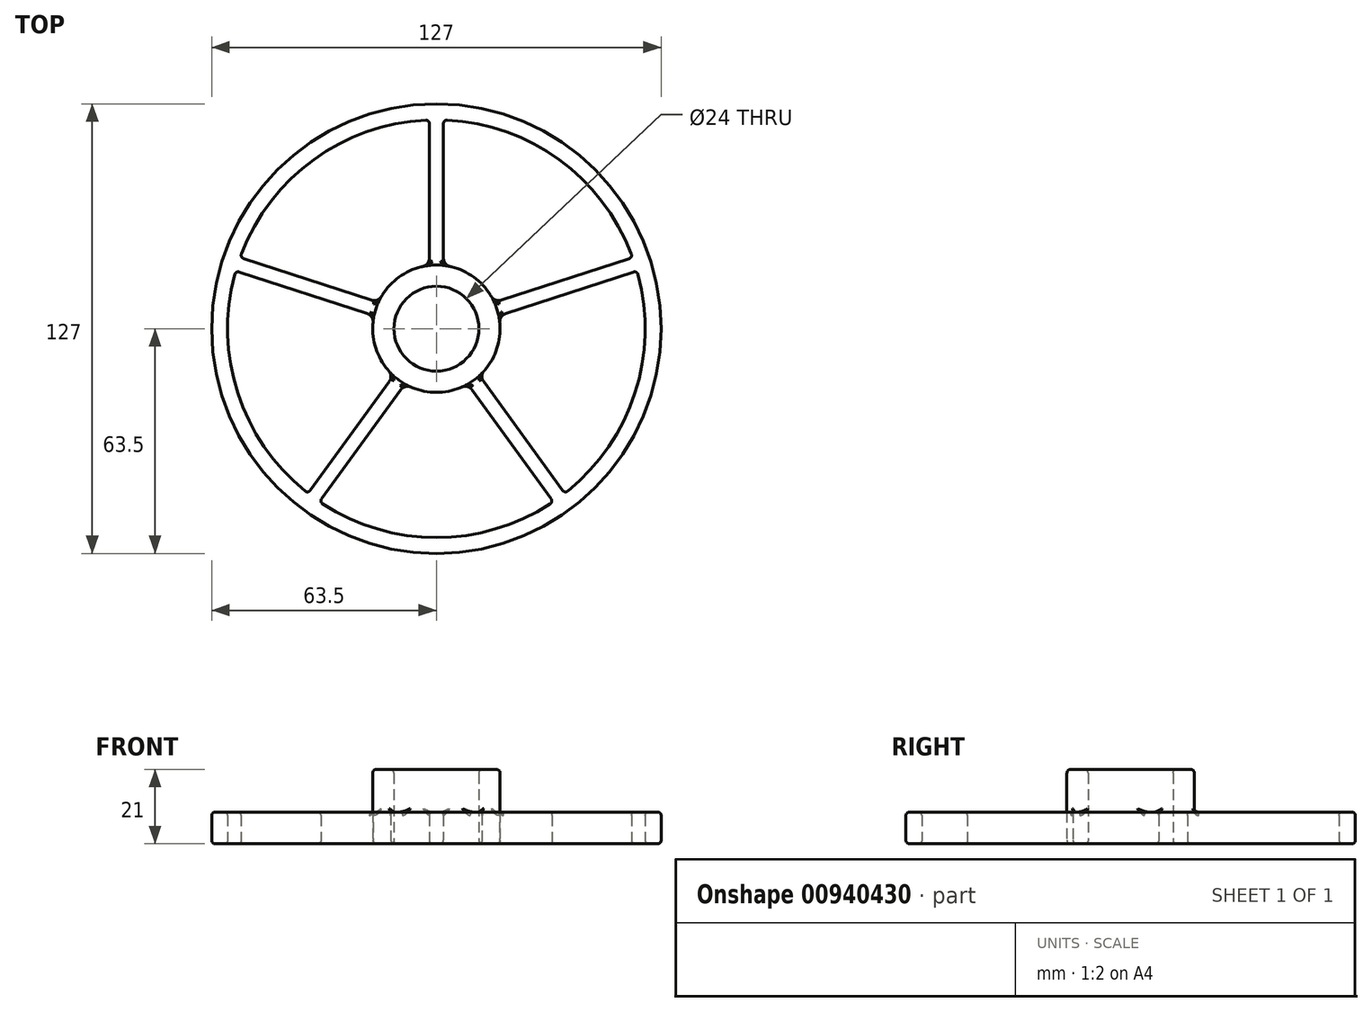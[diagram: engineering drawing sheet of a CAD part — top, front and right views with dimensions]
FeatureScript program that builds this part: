
annotation { "Feature Type Name" : "Feature", "Feature Type Description" : "" }
export const myFeature = defineFeature(function(context is Context, id is Id, definition is map)
    precondition{}
    {
        {
            var Q0;
            Q0=qCreatedBy(makeId("Top.planeOp"),FACE);
            var sketch = newSketch(context, id + "F0", { "sketchPlane" : qUnion([Q0])});
            skCircle(sketch, "E0", {"center": v(0, 0) * mm, "radius": 12 * mm});
            skCircle(sketch, "E1", {"center": v(0, 0) * mm, "radius": 63.5 * mm});
            skArc(sketch, "E2", {"start": v(-2, 58.97) * mm, "mid": v(-34.68, 47.73) * mm, "end": v(-55.46, 20.12) * mm});
            skLineSegment(sketch, "E3.left", {"start": v(-2, 58.97) * mm, "end": v(-2, 19.9) * mm});
            skLineSegment(sketch, "E3.right", {"start": v(2, 58.97) * mm, "end": v(2, 19.92) * mm});
            skPoint(sketch, "E3.middle", {"position": v(0, 38.97) * mm});
            skPoint(sketch, "E4", {"position": v(-2, 19.9) * mm});
            skPoint(sketch, "E5", {"position": v(2, 19.92) * mm});
            skPoint(sketch, "E3.top.start.orphan", {"position": v(-2, 18.97) * mm});
            skPoint(sketch, "E6.orphan", {"position": v(2, 18.97) * mm});
            skLineSegment(sketch, "E7.1.0", {"start": v(-56.7, 16.32) * mm, "end": v(-19.54, 4.25) * mm});
            skLineSegment(sketch, "E7.1.1", {"start": v(-55.46, 20.12) * mm, "end": v(-18.33, 8.06) * mm});
            skLineSegment(sketch, "E7.2.0", {"start": v(-33.04, -48.88) * mm, "end": v(-10.08, -17.27) * mm});
            skLineSegment(sketch, "E7.2.1", {"start": v(-36.28, -46.53) * mm, "end": v(-13.33, -14.94) * mm});
            skLineSegment(sketch, "E7.3.0", {"start": v(36.28, -46.53) * mm, "end": v(13.31, -14.92) * mm});
            skLineSegment(sketch, "E7.3.1", {"start": v(33.04, -48.88) * mm, "end": v(10.1, -17.3) * mm});
            skLineSegment(sketch, "E7.4.0", {"start": v(55.46, 20.12) * mm, "end": v(18.3, 8.05) * mm});
            skLineSegment(sketch, "E7.4.1", {"start": v(56.7, 16.32) * mm, "end": v(19.56, 4.25) * mm});
            skArc(sketch, "E8", {"start": v(-17.89, 2.02) * mm, "mid": v(-17.12, -5.56) * mm, "end": v(-13.28, -12.15) * mm});
            skArc(sketch, "E9", {"start": v(2, 19.92) * mm, "mid": v(2.63, 18.28) * mm, "end": v(4.2, 17.5) * mm});
            skArc(sketch, "E10.MirrorCS", {"start": v(-2, 19.92) * mm, "mid": v(-2.63, 18.28) * mm, "end": v(-4.2, 17.5) * mm});
            skArc(sketch, "E11.1.0", {"start": v(-18.33, 8.06) * mm, "mid": v(-16.57, 8.16) * mm, "end": v(-15.35, 9.4) * mm});
            skArc(sketch, "E11.1.1", {"start": v(-19.56, 4.25) * mm, "mid": v(-18.2, 3.14) * mm, "end": v(-17.94, 1.4) * mm});
            skArc(sketch, "E11.2.0", {"start": v(-13.33, -14.94) * mm, "mid": v(-12.88, -13.24) * mm, "end": v(-13.69, -11.69) * mm});
            skArc(sketch, "E11.2.1", {"start": v(-10.1, -17.3) * mm, "mid": v(-8.62, -16.34) * mm, "end": v(-6.89, -16.63) * mm});
            skArc(sketch, "E11.3.0", {"start": v(10.1, -17.3) * mm, "mid": v(8.62, -16.34) * mm, "end": v(6.89, -16.63) * mm});
            skArc(sketch, "E11.3.1", {"start": v(13.33, -14.94) * mm, "mid": v(12.88, -13.24) * mm, "end": v(13.69, -11.69) * mm});
            skArc(sketch, "E11.4.0", {"start": v(19.56, 4.25) * mm, "mid": v(18.2, 3.14) * mm, "end": v(17.94, 1.4) * mm});
            skArc(sketch, "E11.4.1", {"start": v(18.33, 8.06) * mm, "mid": v(16.57, 8.16) * mm, "end": v(15.35, 9.4) * mm});
            skPoint(sketch, "E12", {"position": v(-15.35, 9.4) * mm});
            skPoint(sketch, "E13", {"position": v(-17.94, 1.4) * mm});
            skPoint(sketch, "E14", {"position": v(-4.2, 17.5) * mm});
            skPoint(sketch, "E15", {"position": v(4.2, 17.5) * mm});
            skArc(sketch, "E16.trimOffspring", {"start": v(-3.6, 17.64) * mm, "mid": v(-10.58, 14.56) * mm, "end": v(-15.66, 8.88) * mm});
            skPoint(sketch, "E17", {"position": v(15.35, 9.4) * mm});
            skPoint(sketch, "E18", {"position": v(17.94, 1.4) * mm});
            skArc(sketch, "E19.trimOffspring", {"start": v(15.66, 8.88) * mm, "mid": v(10.58, 14.56) * mm, "end": v(3.6, 17.64) * mm});
            skPoint(sketch, "E20", {"position": v(-13.69, -11.69) * mm});
            skPoint(sketch, "E21", {"position": v(-6.89, -16.63) * mm});
            skArc(sketch, "E22.trimOffspring", {"start": v(-7.45, -16.39) * mm, "mid": v(0, -18) * mm, "end": v(7.45, -16.39) * mm});
            skPoint(sketch, "E23", {"position": v(13.69, -11.69) * mm});
            skPoint(sketch, "E24", {"position": v(6.89, -16.63) * mm});
            skArc(sketch, "E25.trimOffspring", {"start": v(13.28, -12.15) * mm, "mid": v(17.12, -5.56) * mm, "end": v(17.89, 2.02) * mm});
            skArc(sketch, "E26.trimOffspring", {"start": v(55.46, 20.12) * mm, "mid": v(34.68, 47.73) * mm, "end": v(2, 58.97) * mm});
            skArc(sketch, "E27.trimOffspring", {"start": v(36.28, -46.53) * mm, "mid": v(56.11, -18.23) * mm, "end": v(56.7, 16.32) * mm});
            skArc(sketch, "E28.trimOffspring", {"start": v(-33.04, -48.88) * mm, "mid": v(0, -59) * mm, "end": v(33.04, -48.88) * mm});
            skArc(sketch, "E29.trimOffspring", {"start": v(-56.7, 16.32) * mm, "mid": v(-56.11, -18.23) * mm, "end": v(-36.28, -46.53) * mm});
            skSolve(sketch);
        }
        {
            var Q0;
            Q0=makeQuery(id+"F0.imprint","IMPRINT",FACE,{"disambiguationData":[TD([[makeQuery(id+"F0.imprint","IMPRINT",EDGE,{"derivedFrom":sQuery(id+"F0.wireOp",EDGE,"E1")}),1.0]])]});
            var Q1;
            Q1=makeQuery(id+"F0.imprint","IMPRINT",FACE,{"disambiguationData":[TD([[makeQuery(id+"F0.imprint","IMPRINT",EDGE,{"derivedFrom":sQuery(id+"F0.wireOp",EDGE,"E3.bottom")}),-1.0]])]});
            var Q2;
            {var subQ5=sQuery(id+"F0.wireOp",EDGE,"E7.4.0");Q2=makeQuery(id+"F0.imprint","IMPRINT",FACE,{"disambiguationData":[TD([[makeQuery(id+"F0.imprint","IMPRINT",EDGE,{"derivedFrom":subQ5}),1.0]])]});}
            var Q3;
            {var subQ0=sQuery(id+"F0.wireOp",EDGE,"E7.3.0");Q3=makeQuery(id+"F0.imprint","IMPRINT",FACE,{"disambiguationData":[TD([[makeQuery(id+"F0.imprint","IMPRINT",EDGE,{"derivedFrom":subQ0}),1.0]])]});}
            var Q4;
            {var subQ5=sQuery(id+"F0.wireOp",EDGE,"E7.2.0");Q4=makeQuery(id+"F0.imprint","IMPRINT",FACE,{"disambiguationData":[TD([[makeQuery(id+"F0.imprint","IMPRINT",EDGE,{"derivedFrom":subQ5}),1.0]])]});}
            var Q5;
            {var subQ5=sQuery(id+"F0.wireOp",EDGE,"E7.1.0");Q5=makeQuery(id+"F0.imprint","IMPRINT",FACE,{"disambiguationData":[TD([[makeQuery(id+"F0.imprint","IMPRINT",EDGE,{"derivedFrom":subQ5}),1.0]])]});}
            var Q6;
            Q6=makeQuery(id+"F0.imprint","IMPRINT",FACE,{"disambiguationData":[TD([[makeQuery(id+"F0.imprint","IMPRINT",EDGE,{"derivedFrom":sQuery(id+"F0.wireOp",EDGE,"E0")}),-1.0]])]});
            extrude(context, id + "F1", {"entities" : qUnion([Q0, Q1, Q2, Q3, Q4, Q5, Q6]), "depth" : 9 * mm, "offsetDistance" : 25 * mm});
        }
        {
            var Q0;
            Q0=makeQuery(id+"F1.opExtrude","CAP_FACE",FACE,{"disambiguationData":[OSD([sQuery(id+"F0.wireOp",EDGE,"E0"),sQuery(id+"F0.wireOp",EDGE,"E1"),sQuery(id+"F0.wireOp",EDGE,"E2"),sQuery(id+"F0.wireOp",EDGE,"E3.left"),sQuery(id+"F0.wireOp",EDGE,"E3.right"),sQuery(id+"F0.wireOp",EDGE,"E7.1.0"),sQuery(id+"F0.wireOp",EDGE,"E7.1.1"),sQuery(id+"F0.wireOp",EDGE,"E7.2.0"),sQuery(id+"F0.wireOp",EDGE,"E7.2.1"),sQuery(id+"F0.wireOp",EDGE,"E7.3.0"),sQuery(id+"F0.wireOp",EDGE,"E7.3.1"),sQuery(id+"F0.wireOp",EDGE,"E7.4.0"),sQuery(id+"F0.wireOp",EDGE,"E7.4.1"),sQuery(id+"F0.wireOp",EDGE,"E8"),sQuery(id+"F0.wireOp",EDGE,"E9"),sQuery(id+"F0.wireOp",EDGE,"E10.MirrorCS"),sQuery(id+"F0.wireOp",EDGE,"E11.1.0"),sQuery(id+"F0.wireOp",EDGE,"E11.1.1"),sQuery(id+"F0.wireOp",EDGE,"E11.2.0"),sQuery(id+"F0.wireOp",EDGE,"E11.2.1"),sQuery(id+"F0.wireOp",EDGE,"E11.3.0"),sQuery(id+"F0.wireOp",EDGE,"E11.3.1"),sQuery(id+"F0.wireOp",EDGE,"E11.4.0"),sQuery(id+"F0.wireOp",EDGE,"E11.4.1"),sQuery(id+"F0.wireOp",EDGE,"E16.trimOffspring"),sQuery(id+"F0.wireOp",EDGE,"E19.trimOffspring"),sQuery(id+"F0.wireOp",EDGE,"E22.trimOffspring"),sQuery(id+"F0.wireOp",EDGE,"E25.trimOffspring"),sQuery(id+"F0.wireOp",EDGE,"E26.trimOffspring"),sQuery(id+"F0.wireOp",EDGE,"E27.trimOffspring"),sQuery(id+"F0.wireOp",EDGE,"E28.trimOffspring"),sQuery(id+"F0.wireOp",EDGE,"E29.trimOffspring")])],"isStart":false});
            var sketch = newSketch(context, id + "F2", { "sketchPlane" : qUnion([Q0])});
            skCircle(sketch, "E30", {"center": v(0, 0) * mm, "radius": 18 * mm});
            skSolve(sketch);
        }
        {
            var Q0;
            Q0=makeQuery(id+"F2.imprint","IMPRINT",FACE,{"disambiguationData":[TD([[makeQuery(id+"F2.imprint","IMPRINT",EDGE,{"derivedFrom":makeQuery(id+"F1.opExtrude","CAP_EDGE",EDGE,{"disambiguationData":[OSD([sQuery(id+"F0.wireOp",EDGE,"E0")])],"isStart":false})}),-1.0]])]});
            extrude(context, id + "F3", {"entities" : qUnion([Q0]), "operationType" : NewBodyOperationType.ADD, "depth" : 12 * mm, "offsetDistance" : 25 * mm});
        }
        {
            var Q0;
            Q0=makeQuery(id+"F1.opExtrude","SWEPT_FACE",FACE,{"disambiguationData":[OSD([sQuery(id+"F0.wireOp",EDGE,"E7.4.0")])]});
            var Q1;
            Q1=makeQuery(id+"F1.opExtrude","CAP_EDGE",EDGE,{"disambiguationData":[OSD([sQuery(id+"F0.wireOp",EDGE,"E29.trimOffspring")])],"isStart":false});
            var Q2;
            Q2=makeQuery(id+"F1.opExtrude","CAP_EDGE",EDGE,{"disambiguationData":[OSD([sQuery(id+"F0.wireOp",EDGE,"E7.1.1")])],"isStart":false});
            var Q3;
            Q3=makeQuery(id+"F1.opExtrude","CAP_EDGE",EDGE,{"disambiguationData":[OSD([sQuery(id+"F0.wireOp",EDGE,"E1")])],"isStart":false});
            var Q4;
            Q4=makeQuery(id+"F1.opExtrude","CAP_EDGE",EDGE,{"disambiguationData":[OSD([sQuery(id+"F0.wireOp",EDGE,"E7.1.0")])],"isStart":false});
            var Q5;
            Q5=makeQuery(id+"F1.opExtrude","SWEPT_FACE",FACE,{"disambiguationData":[OSD([sQuery(id+"F0.wireOp",EDGE,"E29.trimOffspring")])]});
            var Q6;
            Q6=makeQuery(id+"F1.opExtrude","SWEPT_FACE",FACE,{"disambiguationData":[OSD([sQuery(id+"F0.wireOp",EDGE,"E7.1.1")])]});
            var Q7;
            Q7=makeQuery(id+"F1.opExtrude","CAP_EDGE",EDGE,{"disambiguationData":[OSD([sQuery(id+"F0.wireOp",EDGE,"E7.4.1")])],"isStart":false});
            var Q8;
            {var subQ0=sQuery(id+"F2.wireOp",EDGE,"E30");Q8=makeQuery(id+"F3.boolean.opBoolean","MERGE",FACE,{"derivedFrom":[makeQuery(id+"F1.opExtrude","SWEPT_FACE",FACE,{"disambiguationData":[OSD([sQuery(id+"F0.wireOp",EDGE,"E25.trimOffspring")])]}),makeQuery(id+"F3.opExtrude","SWEPT_FACE",FACE,{"disambiguationData":[OSD([subQ0]),TDD([makeQuery(id+"F2.imprint","IMPRINT",EDGE,{"disambiguationData":[TD([[makeQuery(id+"F2.imprint","INTERSECT",VERTEX,{"disambiguationData":[OD(0.0)],"derivedFrom":[makeQuery(id+"F1.opExtrude","CAP_EDGE",EDGE,{"disambiguationData":[OSD([sQuery(id+"F0.wireOp",EDGE,"E11.3.1")])],"isStart":false}),subQ0]}),-1.0]])],"derivedFrom":subQ0})])]})]});}
            var Q9;
            Q9=makeQuery(id+"F1.opExtrude","SWEPT_FACE",FACE,{"disambiguationData":[OSD([sQuery(id+"F0.wireOp",EDGE,"E7.2.1")])]});
            var Q10;
            Q10=makeQuery(id+"F1.opExtrude","CAP_EDGE",EDGE,{"disambiguationData":[OSD([sQuery(id+"F0.wireOp",EDGE,"E2")])],"isStart":false});
            var Q11;
            Q11=makeQuery(id+"F1.opExtrude","SWEPT_FACE",FACE,{"disambiguationData":[OSD([sQuery(id+"F0.wireOp",EDGE,"E3.left")])]});
            var Q12;
            Q12=makeQuery(id+"F1.opExtrude","CAP_EDGE",EDGE,{"disambiguationData":[OSD([sQuery(id+"F0.wireOp",EDGE,"E27.trimOffspring")])],"isStart":false});
            var Q13;
            Q13=makeQuery(id+"F1.opExtrude","SWEPT_FACE",FACE,{"disambiguationData":[OSD([sQuery(id+"F0.wireOp",EDGE,"E7.3.0")])]});
            var Q14;
            Q14=makeQuery(id+"F1.opExtrude","CAP_EDGE",EDGE,{"disambiguationData":[OSD([sQuery(id+"F0.wireOp",EDGE,"E26.trimOffspring")])],"isStart":false});
            var Q15;
            Q15=makeQuery(id+"F1.opExtrude","SWEPT_FACE",FACE,{"disambiguationData":[OSD([sQuery(id+"F0.wireOp",EDGE,"E3.right")])]});
            var Q16;
            {var subQ0=sQuery(id+"F2.wireOp",EDGE,"E30");Q16=makeQuery(id+"F3.opExtrude","SWEPT_FACE",FACE,{"disambiguationData":[OSD([subQ0]),TDD([makeQuery(id+"F2.imprint","IMPRINT",EDGE,{"disambiguationData":[TD([[makeQuery(id+"F2.imprint","INTERSECT",VERTEX,{"disambiguationData":[OD(1.0)],"derivedFrom":[makeQuery(id+"F1.opExtrude","CAP_EDGE",EDGE,{"disambiguationData":[OSD([sQuery(id+"F0.wireOp",EDGE,"E11.1.0")])],"isStart":false}),subQ0]}),-1.0]])],"derivedFrom":subQ0})])]});}
            var Q17;
            Q17=makeQuery(id+"F1.opExtrude","SWEPT_FACE",FACE,{"disambiguationData":[OSD([sQuery(id+"F0.wireOp",EDGE,"E7.1.0")])]});
            var Q18;
            Q18=makeQuery(id+"F1.opExtrude","SWEPT_FACE",FACE,{"disambiguationData":[OSD([sQuery(id+"F0.wireOp",EDGE,"E2")])]});
            var Q19;
            {var subQ0=sQuery(id+"F0.wireOp",EDGE,"E11.4.0");Q19=makeQuery(id+"F3.boolean.opBoolean","MERGE",FACE,{"derivedFrom":[makeQuery(id+"F1.opExtrude","SWEPT_FACE",FACE,{"disambiguationData":[OSD([subQ0])]}),makeQuery(id+"F3.opExtrude","SWEPT_FACE",FACE,{"disambiguationData":[OSD([subQ0])]})]});}
            var Q20;
            Q20=makeQuery(id+"F1.opExtrude","CAP_EDGE",EDGE,{"disambiguationData":[OSD([sQuery(id+"F0.wireOp",EDGE,"E3.left")])],"isStart":false});
            var Q21;
            Q21=makeQuery(id+"F3.opExtrude","CAP_FACE",FACE,{"disambiguationData":[OSD([sQuery(id+"F0.wireOp",EDGE,"E0"),sQuery(id+"F0.wireOp",EDGE,"E9"),sQuery(id+"F0.wireOp",EDGE,"E10.MirrorCS"),sQuery(id+"F0.wireOp",EDGE,"E11.1.0"),sQuery(id+"F0.wireOp",EDGE,"E11.1.1"),sQuery(id+"F0.wireOp",EDGE,"E11.2.0"),sQuery(id+"F0.wireOp",EDGE,"E11.2.1"),sQuery(id+"F0.wireOp",EDGE,"E11.3.0"),sQuery(id+"F0.wireOp",EDGE,"E11.3.1"),sQuery(id+"F0.wireOp",EDGE,"E11.4.0"),sQuery(id+"F0.wireOp",EDGE,"E11.4.1"),sQuery(id+"F2.wireOp",EDGE,"E30")])],"isStart":false});
            var Q22;
            Q22=makeQuery(id+"F1.opExtrude","SWEPT_FACE",FACE,{"disambiguationData":[OSD([sQuery(id+"F0.wireOp",EDGE,"E28.trimOffspring")])]});
            var Q23;
            Q23=makeQuery(id+"F1.opExtrude","SWEPT_FACE",FACE,{"disambiguationData":[OSD([sQuery(id+"F0.wireOp",EDGE,"E7.2.0")])]});
            var Q24;
            Q24=makeQuery(id+"F1.opExtrude","SWEPT_FACE",FACE,{"disambiguationData":[OSD([sQuery(id+"F0.wireOp",EDGE,"E7.4.1")])]});
            var Q25;
            Q25=makeQuery(id+"F1.opExtrude","CAP_EDGE",EDGE,{"disambiguationData":[OSD([sQuery(id+"F0.wireOp",EDGE,"E3.right")])],"isStart":false});
            var Q26;
            Q26=makeQuery(id+"F1.opExtrude","SWEPT_FACE",FACE,{"disambiguationData":[OSD([sQuery(id+"F0.wireOp",EDGE,"E27.trimOffspring")])]});
            var Q27;
            Q27=makeQuery(id+"F1.opExtrude","SWEPT_FACE",FACE,{"disambiguationData":[OSD([sQuery(id+"F0.wireOp",EDGE,"E7.3.1")])]});
            var Q28;
            Q28=makeQuery(id+"F1.opExtrude","SWEPT_FACE",FACE,{"disambiguationData":[OSD([sQuery(id+"F0.wireOp",EDGE,"E26.trimOffspring")])]});
            var Q29;
            Q29=makeQuery(id+"F1.opExtrude","SWEPT_FACE",FACE,{"disambiguationData":[OSD([sQuery(id+"F0.wireOp",EDGE,"E1")])]});
            var Q30;
            Q30=makeQuery(id+"F1.opExtrude","CAP_EDGE",EDGE,{"disambiguationData":[OSD([sQuery(id+"F0.wireOp",EDGE,"E28.trimOffspring")])],"isStart":false});
            var Q31;
            {var subQ0=sQuery(id+"F2.wireOp",EDGE,"E30");Q31=makeQuery(id+"F3.boolean.opBoolean","MERGE",FACE,{"derivedFrom":[makeQuery(id+"F1.opExtrude","SWEPT_FACE",FACE,{"disambiguationData":[OSD([sQuery(id+"F0.wireOp",EDGE,"E8")])]}),makeQuery(id+"F3.opExtrude","SWEPT_FACE",FACE,{"disambiguationData":[OSD([subQ0]),TDD([makeQuery(id+"F2.imprint","IMPRINT",EDGE,{"disambiguationData":[TD([[makeQuery(id+"F2.imprint","INTERSECT",VERTEX,{"disambiguationData":[OD(0.0)],"derivedFrom":[makeQuery(id+"F1.opExtrude","CAP_EDGE",EDGE,{"disambiguationData":[OSD([sQuery(id+"F0.wireOp",EDGE,"E11.1.1")])],"isStart":false}),subQ0]}),-1.0]])],"derivedFrom":subQ0})])]})]});}
            var Q32;
            Q32=makeQuery(id+"F1.opExtrude","CAP_FACE",FACE,{"disambiguationData":[OSD([sQuery(id+"F0.wireOp",EDGE,"E0"),sQuery(id+"F0.wireOp",EDGE,"E1"),sQuery(id+"F0.wireOp",EDGE,"E2"),sQuery(id+"F0.wireOp",EDGE,"E3.left"),sQuery(id+"F0.wireOp",EDGE,"E3.right"),sQuery(id+"F0.wireOp",EDGE,"E7.1.0"),sQuery(id+"F0.wireOp",EDGE,"E7.1.1"),sQuery(id+"F0.wireOp",EDGE,"E7.2.0"),sQuery(id+"F0.wireOp",EDGE,"E7.2.1"),sQuery(id+"F0.wireOp",EDGE,"E7.3.0"),sQuery(id+"F0.wireOp",EDGE,"E7.3.1"),sQuery(id+"F0.wireOp",EDGE,"E7.4.0"),sQuery(id+"F0.wireOp",EDGE,"E7.4.1"),sQuery(id+"F0.wireOp",EDGE,"E8"),sQuery(id+"F0.wireOp",EDGE,"E9"),sQuery(id+"F0.wireOp",EDGE,"E10.MirrorCS"),sQuery(id+"F0.wireOp",EDGE,"E11.1.0"),sQuery(id+"F0.wireOp",EDGE,"E11.1.1"),sQuery(id+"F0.wireOp",EDGE,"E11.2.0"),sQuery(id+"F0.wireOp",EDGE,"E11.2.1"),sQuery(id+"F0.wireOp",EDGE,"E11.3.0"),sQuery(id+"F0.wireOp",EDGE,"E11.3.1"),sQuery(id+"F0.wireOp",EDGE,"E11.4.0"),sQuery(id+"F0.wireOp",EDGE,"E11.4.1"),sQuery(id+"F0.wireOp",EDGE,"E16.trimOffspring"),sQuery(id+"F0.wireOp",EDGE,"E19.trimOffspring"),sQuery(id+"F0.wireOp",EDGE,"E22.trimOffspring"),sQuery(id+"F0.wireOp",EDGE,"E25.trimOffspring"),sQuery(id+"F0.wireOp",EDGE,"E26.trimOffspring"),sQuery(id+"F0.wireOp",EDGE,"E27.trimOffspring"),sQuery(id+"F0.wireOp",EDGE,"E28.trimOffspring"),sQuery(id+"F0.wireOp",EDGE,"E29.trimOffspring")])],"isStart":false});
            var Q33;
            {var subQ0=sQuery(id+"F2.wireOp",EDGE,"E30");Q33=makeQuery(id+"F3.boolean.opBoolean","MERGE",FACE,{"derivedFrom":[makeQuery(id+"F1.opExtrude","SWEPT_FACE",FACE,{"disambiguationData":[OSD([sQuery(id+"F0.wireOp",EDGE,"E19.trimOffspring")])]}),makeQuery(id+"F3.opExtrude","SWEPT_FACE",FACE,{"disambiguationData":[OSD([subQ0]),TDD([makeQuery(id+"F2.imprint","IMPRINT",EDGE,{"disambiguationData":[TD([[makeQuery(id+"F2.imprint","INTERSECT",VERTEX,{"disambiguationData":[OD(0.0)],"derivedFrom":[makeQuery(id+"F1.opExtrude","CAP_EDGE",EDGE,{"disambiguationData":[OSD([sQuery(id+"F0.wireOp",EDGE,"E9")])],"isStart":false}),subQ0]}),1.0]])],"derivedFrom":subQ0})])]})]});}
            var Q34;
            {var subQ0=sQuery(id+"F0.wireOp",EDGE,"E0");Q34=makeQuery(id+"F3.boolean.opBoolean","MERGE",FACE,{"derivedFrom":[makeQuery(id+"F1.opExtrude","SWEPT_FACE",FACE,{"disambiguationData":[OSD([subQ0])]}),makeQuery(id+"F3.opExtrude","SWEPT_FACE",FACE,{"disambiguationData":[OSD([subQ0])]})]});}
            var Q35;
            {var subQ0=sQuery(id+"F2.wireOp",EDGE,"E30");Q35=makeQuery(id+"F3.opExtrude","SWEPT_FACE",FACE,{"disambiguationData":[OSD([subQ0]),TDD([makeQuery(id+"F2.imprint","IMPRINT",EDGE,{"disambiguationData":[TD([[makeQuery(id+"F2.imprint","INTERSECT",VERTEX,{"disambiguationData":[OD(1.0)],"derivedFrom":[makeQuery(id+"F1.opExtrude","CAP_EDGE",EDGE,{"disambiguationData":[OSD([sQuery(id+"F0.wireOp",EDGE,"E9")])],"isStart":false}),subQ0]}),-1.0]])],"derivedFrom":subQ0})])]});}
            var Q36;
            {var subQ0=sQuery(id+"F2.wireOp",EDGE,"E30");Q36=makeQuery(id+"F3.boolean.opBoolean","MERGE",FACE,{"derivedFrom":[makeQuery(id+"F1.opExtrude","SWEPT_FACE",FACE,{"disambiguationData":[OSD([sQuery(id+"F0.wireOp",EDGE,"E22.trimOffspring")])]}),makeQuery(id+"F3.opExtrude","SWEPT_FACE",FACE,{"disambiguationData":[OSD([subQ0]),TDD([makeQuery(id+"F2.imprint","IMPRINT",EDGE,{"disambiguationData":[TD([[makeQuery(id+"F2.imprint","INTERSECT",VERTEX,{"disambiguationData":[OD(0.0)],"derivedFrom":[makeQuery(id+"F1.opExtrude","CAP_EDGE",EDGE,{"disambiguationData":[OSD([sQuery(id+"F0.wireOp",EDGE,"E11.2.1")])],"isStart":false}),subQ0]}),-1.0]])],"derivedFrom":subQ0})])]})]});}
            var Q37;
            Q37=makeQuery(id+"F1.opExtrude","CAP_EDGE",EDGE,{"disambiguationData":[OSD([sQuery(id+"F0.wireOp",EDGE,"E7.4.0")])],"isStart":true});
            var Q38;
            Q38=makeQuery(id+"F1.opExtrude","CAP_EDGE",EDGE,{"disambiguationData":[OSD([sQuery(id+"F0.wireOp",EDGE,"E7.3.1")])],"isStart":false});
            var Q39;
            Q39=makeQuery(id+"F1.opExtrude","SWEPT_EDGE",EDGE,{"disambiguationData":[OSD([sQuery(id+"F0.wireOp",EDGE,"E3.right"),sQuery(id+"F0.wireOp",EDGE,"E26.trimOffspring")])]});
            var Q40;
            Q40=makeQuery(id+"F1.opExtrude","CAP_EDGE",EDGE,{"disambiguationData":[OSD([sQuery(id+"F0.wireOp",EDGE,"E1")])],"isStart":true});
            var Q41;
            Q41=makeQuery(id+"F1.opExtrude","CAP_EDGE",EDGE,{"disambiguationData":[OSD([sQuery(id+"F0.wireOp",EDGE,"E26.trimOffspring")])],"isStart":true});
            var Q42;
            {var subQ0=sQuery(id+"F0.wireOp",EDGE,"E11.4.1");Q42=makeQuery(id+"F3.boolean.opBoolean","MERGE",FACE,{"derivedFrom":[makeQuery(id+"F1.opExtrude","SWEPT_FACE",FACE,{"disambiguationData":[OSD([subQ0])]}),makeQuery(id+"F3.opExtrude","SWEPT_FACE",FACE,{"disambiguationData":[OSD([subQ0])]})]});}
            var Q43;
            Q43=makeQuery(id+"F1.opExtrude","CAP_EDGE",EDGE,{"disambiguationData":[OSD([sQuery(id+"F0.wireOp",EDGE,"E7.3.0")])],"isStart":false});
            var Q44;
            Q44=makeQuery(id+"F1.opExtrude","CAP_EDGE",EDGE,{"disambiguationData":[OSD([sQuery(id+"F0.wireOp",EDGE,"E7.4.1")])],"isStart":true});
            var Q45;
            Q45=makeQuery(id+"F1.opExtrude","CAP_EDGE",EDGE,{"disambiguationData":[OSD([sQuery(id+"F0.wireOp",EDGE,"E28.trimOffspring")])],"isStart":true});
            var Q46;
            Q46=makeQuery(id+"F1.opExtrude","CAP_EDGE",EDGE,{"disambiguationData":[OSD([sQuery(id+"F0.wireOp",EDGE,"E7.2.0")])],"isStart":false});
            var Q47;
            Q47=makeQuery(id+"F1.opExtrude","CAP_EDGE",EDGE,{"disambiguationData":[OSD([sQuery(id+"F0.wireOp",EDGE,"E7.2.1")])],"isStart":false});
            var Q48;
            Q48=makeQuery(id+"F1.opExtrude","CAP_EDGE",EDGE,{"disambiguationData":[OSD([sQuery(id+"F0.wireOp",EDGE,"E7.2.0")])],"isStart":true});
            var Q49;
            {var subQ0=sQuery(id+"F0.wireOp",EDGE,"E11.3.1");Q49=makeQuery(id+"F3.boolean.opBoolean","MERGE",FACE,{"derivedFrom":[makeQuery(id+"F1.opExtrude","SWEPT_FACE",FACE,{"disambiguationData":[OSD([subQ0])]}),makeQuery(id+"F3.opExtrude","SWEPT_FACE",FACE,{"disambiguationData":[OSD([subQ0])]})]});}
            var Q50;
            Q50=makeQuery(id+"F1.opExtrude","CAP_EDGE",EDGE,{"disambiguationData":[OSD([sQuery(id+"F0.wireOp",EDGE,"E29.trimOffspring")])],"isStart":true});
            var Q51;
            {var subQ0=sQuery(id+"F2.wireOp",EDGE,"E30");Q51=makeQuery(id+"F3.opExtrude","CAP_EDGE",EDGE,{"disambiguationData":[OSD([subQ0]),TDD([makeQuery(id+"F2.imprint","IMPRINT",EDGE,{"disambiguationData":[TD([[makeQuery(id+"F2.imprint","INTERSECT",VERTEX,{"disambiguationData":[OD(0.0)],"derivedFrom":[makeQuery(id+"F1.opExtrude","CAP_EDGE",EDGE,{"disambiguationData":[OSD([sQuery(id+"F0.wireOp",EDGE,"E11.1.1")])],"isStart":false}),subQ0]}),-1.0]])],"derivedFrom":subQ0})])],"isStart":false});}
            var Q52;
            Q52=makeQuery(id+"F1.opExtrude","SWEPT_EDGE",EDGE,{"disambiguationData":[OSD([sQuery(id+"F0.wireOp",EDGE,"E7.4.0"),sQuery(id+"F0.wireOp",EDGE,"E26.trimOffspring")])]});
            var Q53;
            Q53=makeQuery(id+"F1.opExtrude","CAP_EDGE",EDGE,{"disambiguationData":[OSD([sQuery(id+"F0.wireOp",EDGE,"E7.1.1")])],"isStart":true});
            var Q54;
            Q54=makeQuery(id+"F1.opExtrude","CAP_EDGE",EDGE,{"disambiguationData":[OSD([sQuery(id+"F0.wireOp",EDGE,"E7.1.0")])],"isStart":true});
            var Q55;
            Q55=makeQuery(id+"F1.opExtrude","SWEPT_EDGE",EDGE,{"disambiguationData":[OSD([sQuery(id+"F0.wireOp",EDGE,"E7.1.0"),sQuery(id+"F0.wireOp",EDGE,"E29.trimOffspring")])]});
            var Q56;
            Q56=makeQuery(id+"F1.opExtrude","CAP_EDGE",EDGE,{"disambiguationData":[OSD([sQuery(id+"F0.wireOp",EDGE,"E7.4.0")])],"isStart":false});
            var Q57;
            {var subQ0=sQuery(id+"F2.wireOp",EDGE,"E30");Q57=makeQuery(id+"F3.opExtrude","CAP_EDGE",EDGE,{"disambiguationData":[OSD([subQ0]),TDD([makeQuery(id+"F2.imprint","IMPRINT",EDGE,{"disambiguationData":[TD([[makeQuery(id+"F2.imprint","INTERSECT",VERTEX,{"disambiguationData":[OD(0.0)],"derivedFrom":[makeQuery(id+"F1.opExtrude","CAP_EDGE",EDGE,{"disambiguationData":[OSD([sQuery(id+"F0.wireOp",EDGE,"E9")])],"isStart":false}),subQ0]}),1.0]])],"derivedFrom":subQ0})])],"isStart":false});}
            var Q58;
            {var subQ0=sQuery(id+"F2.wireOp",EDGE,"E30");Q58=makeQuery(id+"F3.opExtrude","CAP_EDGE",EDGE,{"disambiguationData":[OSD([subQ0]),TDD([makeQuery(id+"F2.imprint","IMPRINT",EDGE,{"disambiguationData":[TD([[makeQuery(id+"F2.imprint","INTERSECT",VERTEX,{"disambiguationData":[OD(0.0)],"derivedFrom":[makeQuery(id+"F1.opExtrude","CAP_EDGE",EDGE,{"disambiguationData":[OSD([sQuery(id+"F0.wireOp",EDGE,"E11.2.1")])],"isStart":false}),subQ0]}),-1.0]])],"derivedFrom":subQ0})])],"isStart":false});}
            var Q59;
            Q59=makeQuery(id+"F1.opExtrude","CAP_EDGE",EDGE,{"disambiguationData":[OSD([sQuery(id+"F0.wireOp",EDGE,"E7.2.1")])],"isStart":true});
            var Q60;
            Q60=makeQuery(id+"F1.opExtrude","SWEPT_EDGE",EDGE,{"disambiguationData":[OSD([sQuery(id+"F0.wireOp",EDGE,"E7.4.1"),sQuery(id+"F0.wireOp",EDGE,"E11.4.0")])]});
            var Q61;
            Q61=makeQuery(id+"F1.opExtrude","CAP_EDGE",EDGE,{"disambiguationData":[OSD([sQuery(id+"F0.wireOp",EDGE,"E27.trimOffspring")])],"isStart":true});
            var Q62;
            Q62=makeQuery(id+"F1.opExtrude","SWEPT_EDGE",EDGE,{"disambiguationData":[OSD([sQuery(id+"F0.wireOp",EDGE,"E7.2.1"),sQuery(id+"F0.wireOp",EDGE,"E29.trimOffspring")])]});
            var Q63;
            {var subQ0=sQuery(id+"F0.wireOp",EDGE,"E9");Q63=makeQuery(id+"F3.boolean.opBoolean","MERGE",FACE,{"derivedFrom":[makeQuery(id+"F1.opExtrude","SWEPT_FACE",FACE,{"disambiguationData":[OSD([subQ0])]}),makeQuery(id+"F3.opExtrude","SWEPT_FACE",FACE,{"disambiguationData":[OSD([subQ0])]})]});}
            var Q64;
            Q64=makeQuery(id+"F1.opExtrude","CAP_EDGE",EDGE,{"disambiguationData":[OSD([sQuery(id+"F0.wireOp",EDGE,"E3.left")])],"isStart":true});
            var Q65;
            Q65=makeQuery(id+"F1.opExtrude","SWEPT_EDGE",EDGE,{"disambiguationData":[OSD([sQuery(id+"F0.wireOp",EDGE,"E7.4.1"),sQuery(id+"F0.wireOp",EDGE,"E27.trimOffspring")])]});
            var Q66;
            Q66=makeQuery(id+"F1.opExtrude","CAP_EDGE",EDGE,{"disambiguationData":[OSD([sQuery(id+"F0.wireOp",EDGE,"E2")])],"isStart":true});
            var Q67;
            {var subQ0=sQuery(id+"F0.wireOp",EDGE,"E11.1.0");Q67=makeQuery(id+"F3.boolean.opBoolean","MERGE",FACE,{"derivedFrom":[makeQuery(id+"F1.opExtrude","SWEPT_FACE",FACE,{"disambiguationData":[OSD([subQ0])]}),makeQuery(id+"F3.opExtrude","SWEPT_FACE",FACE,{"disambiguationData":[OSD([subQ0])]})]});}
            var Q68;
            Q68=makeQuery(id+"F1.opExtrude","SWEPT_EDGE",EDGE,{"disambiguationData":[OSD([sQuery(id+"F0.wireOp",EDGE,"E2"),sQuery(id+"F0.wireOp",EDGE,"E3.left")])]});
            var Q69;
            Q69=makeQuery(id+"F1.opExtrude","CAP_EDGE",EDGE,{"disambiguationData":[OSD([sQuery(id+"F0.wireOp",EDGE,"E3.right")])],"isStart":true});
            var Q70;
            Q70=makeQuery(id+"F1.opExtrude","SWEPT_EDGE",EDGE,{"disambiguationData":[OSD([sQuery(id+"F0.wireOp",EDGE,"E2"),sQuery(id+"F0.wireOp",EDGE,"E7.1.1")])]});
            var Q71;
            {var subQ0=sQuery(id+"F0.wireOp",EDGE,"E10.MirrorCS");Q71=makeQuery(id+"F3.boolean.opBoolean","MERGE",FACE,{"derivedFrom":[makeQuery(id+"F1.opExtrude","SWEPT_FACE",FACE,{"disambiguationData":[OSD([subQ0])]}),makeQuery(id+"F3.opExtrude","SWEPT_FACE",FACE,{"disambiguationData":[OSD([subQ0])]})]});}
            var Q72;
            {var subQ0=sQuery(id+"F0.wireOp",EDGE,"E11.3.0");Q72=makeQuery(id+"F3.boolean.opBoolean","MERGE",FACE,{"derivedFrom":[makeQuery(id+"F1.opExtrude","SWEPT_FACE",FACE,{"disambiguationData":[OSD([subQ0])]}),makeQuery(id+"F3.opExtrude","SWEPT_FACE",FACE,{"disambiguationData":[OSD([subQ0])]})]});}
            var Q73;
            {var subQ0=sQuery(id+"F2.wireOp",EDGE,"E30");Q73=makeQuery(id+"F3.opExtrude","SWEPT_FACE",FACE,{"disambiguationData":[OSD([subQ0]),TDD([makeQuery(id+"F2.imprint","IMPRINT",EDGE,{"disambiguationData":[TD([[makeQuery(id+"F2.imprint","INTERSECT",VERTEX,{"disambiguationData":[OD(1.0)],"derivedFrom":[makeQuery(id+"F1.opExtrude","CAP_EDGE",EDGE,{"disambiguationData":[OSD([sQuery(id+"F0.wireOp",EDGE,"E11.4.0")])],"isStart":false}),subQ0]}),-1.0]])],"derivedFrom":subQ0})])]});}
            var Q74;
            {var subQ0=sQuery(id+"F2.wireOp",EDGE,"E30");Q74=makeQuery(id+"F3.opExtrude","SWEPT_FACE",FACE,{"disambiguationData":[OSD([subQ0]),TDD([makeQuery(id+"F2.imprint","IMPRINT",EDGE,{"disambiguationData":[TD([[makeQuery(id+"F2.imprint","INTERSECT",VERTEX,{"disambiguationData":[OD(1.0)],"derivedFrom":[makeQuery(id+"F1.opExtrude","CAP_EDGE",EDGE,{"disambiguationData":[OSD([sQuery(id+"F0.wireOp",EDGE,"E11.3.0")])],"isStart":false}),subQ0]}),-1.0]])],"derivedFrom":subQ0})])]});}
            var Q75;
            {var subQ0=sQuery(id+"F0.wireOp",EDGE,"E11.2.1");Q75=makeQuery(id+"F3.boolean.opBoolean","MERGE",FACE,{"derivedFrom":[makeQuery(id+"F1.opExtrude","SWEPT_FACE",FACE,{"disambiguationData":[OSD([subQ0])]}),makeQuery(id+"F3.opExtrude","SWEPT_FACE",FACE,{"disambiguationData":[OSD([subQ0])]})]});}
            var Q76;
            Q76=makeQuery(id+"F3.opExtrude","CAP_EDGE",EDGE,{"disambiguationData":[OSD([sQuery(id+"F0.wireOp",EDGE,"E11.4.0")])],"isStart":false});
            var Q77;
            Q77=makeQuery(id+"F1.opExtrude","CAP_FACE",FACE,{"disambiguationData":[OSD([sQuery(id+"F0.wireOp",EDGE,"E0"),sQuery(id+"F0.wireOp",EDGE,"E1"),sQuery(id+"F0.wireOp",EDGE,"E2"),sQuery(id+"F0.wireOp",EDGE,"E3.left"),sQuery(id+"F0.wireOp",EDGE,"E3.right"),sQuery(id+"F0.wireOp",EDGE,"E7.1.0"),sQuery(id+"F0.wireOp",EDGE,"E7.1.1"),sQuery(id+"F0.wireOp",EDGE,"E7.2.0"),sQuery(id+"F0.wireOp",EDGE,"E7.2.1"),sQuery(id+"F0.wireOp",EDGE,"E7.3.0"),sQuery(id+"F0.wireOp",EDGE,"E7.3.1"),sQuery(id+"F0.wireOp",EDGE,"E7.4.0"),sQuery(id+"F0.wireOp",EDGE,"E7.4.1"),sQuery(id+"F0.wireOp",EDGE,"E8"),sQuery(id+"F0.wireOp",EDGE,"E9"),sQuery(id+"F0.wireOp",EDGE,"E10.MirrorCS"),sQuery(id+"F0.wireOp",EDGE,"E11.1.0"),sQuery(id+"F0.wireOp",EDGE,"E11.1.1"),sQuery(id+"F0.wireOp",EDGE,"E11.2.0"),sQuery(id+"F0.wireOp",EDGE,"E11.2.1"),sQuery(id+"F0.wireOp",EDGE,"E11.3.0"),sQuery(id+"F0.wireOp",EDGE,"E11.3.1"),sQuery(id+"F0.wireOp",EDGE,"E11.4.0"),sQuery(id+"F0.wireOp",EDGE,"E11.4.1"),sQuery(id+"F0.wireOp",EDGE,"E16.trimOffspring"),sQuery(id+"F0.wireOp",EDGE,"E19.trimOffspring"),sQuery(id+"F0.wireOp",EDGE,"E22.trimOffspring"),sQuery(id+"F0.wireOp",EDGE,"E25.trimOffspring"),sQuery(id+"F0.wireOp",EDGE,"E26.trimOffspring"),sQuery(id+"F0.wireOp",EDGE,"E27.trimOffspring"),sQuery(id+"F0.wireOp",EDGE,"E28.trimOffspring"),sQuery(id+"F0.wireOp",EDGE,"E29.trimOffspring")])],"isStart":true});
            var Q78;
            {var subQ0=sQuery(id+"F2.wireOp",EDGE,"E30");var subQ1=sQuery(id+"F0.wireOp",EDGE,"E11.2.0");Q78=makeQuery(id+"F3.boolean.opBoolean","MERGE",EDGE,{"derivedFrom":[makeQuery(id+"F1.opExtrude","SWEPT_EDGE",EDGE,{"disambiguationData":[OSD([sQuery(id+"F0.wireOp",EDGE,"E8"),subQ1])]}),makeQuery(id+"F3.opExtrude","SWEPT_EDGE",EDGE,{"disambiguationData":[OSD([subQ1,subQ0]),TDD([makeQuery(id+"F2.imprint","INTERSECT",VERTEX,{"disambiguationData":[OD(0.0)],"derivedFrom":[makeQuery(id+"F1.opExtrude","CAP_EDGE",EDGE,{"disambiguationData":[OSD([subQ1])],"isStart":false}),subQ0]})])]})]});}
            var Q79;
            {var subQ0=sQuery(id+"F2.wireOp",EDGE,"E30");Q79=makeQuery(id+"F3.opExtrude","CAP_EDGE",EDGE,{"disambiguationData":[OSD([subQ0]),TDD([makeQuery(id+"F2.imprint","IMPRINT",EDGE,{"disambiguationData":[TD([[makeQuery(id+"F2.imprint","INTERSECT",VERTEX,{"disambiguationData":[OD(1.0)],"derivedFrom":[makeQuery(id+"F1.opExtrude","CAP_EDGE",EDGE,{"disambiguationData":[OSD([sQuery(id+"F0.wireOp",EDGE,"E9")])],"isStart":false}),subQ0]}),-1.0]])],"derivedFrom":subQ0})])],"isStart":false});}
            var Q80;
            {var subQ0=sQuery(id+"F2.wireOp",EDGE,"E30");Q80=makeQuery(id+"F3.opExtrude","CAP_EDGE",EDGE,{"disambiguationData":[OSD([subQ0]),TDD([makeQuery(id+"F2.imprint","IMPRINT",EDGE,{"disambiguationData":[TD([[makeQuery(id+"F2.imprint","INTERSECT",VERTEX,{"disambiguationData":[OD(1.0)],"derivedFrom":[makeQuery(id+"F1.opExtrude","CAP_EDGE",EDGE,{"disambiguationData":[OSD([sQuery(id+"F0.wireOp",EDGE,"E11.1.0")])],"isStart":false}),subQ0]}),-1.0]])],"derivedFrom":subQ0})])],"isStart":false});}
            var Q81;
            {var subQ0=sQuery(id+"F2.wireOp",EDGE,"E30");Q81=makeQuery(id+"F3.boolean.opBoolean","MERGE",FACE,{"derivedFrom":[makeQuery(id+"F1.opExtrude","SWEPT_FACE",FACE,{"disambiguationData":[OSD([sQuery(id+"F0.wireOp",EDGE,"E16.trimOffspring")])]}),makeQuery(id+"F3.opExtrude","SWEPT_FACE",FACE,{"disambiguationData":[OSD([subQ0]),TDD([makeQuery(id+"F2.imprint","IMPRINT",EDGE,{"disambiguationData":[TD([[makeQuery(id+"F2.imprint","INTERSECT",VERTEX,{"disambiguationData":[OD(0.0)],"derivedFrom":[makeQuery(id+"F1.opExtrude","CAP_EDGE",EDGE,{"disambiguationData":[OSD([sQuery(id+"F0.wireOp",EDGE,"E10.MirrorCS")])],"isStart":false}),subQ0]}),-1.0]])],"derivedFrom":subQ0})])]})]});}
            var Q82;
            {var subQ0=sQuery(id+"F0.wireOp",EDGE,"E11.1.1");Q82=makeQuery(id+"F3.boolean.opBoolean","MERGE",FACE,{"derivedFrom":[makeQuery(id+"F1.opExtrude","SWEPT_FACE",FACE,{"disambiguationData":[OSD([subQ0])]}),makeQuery(id+"F3.opExtrude","SWEPT_FACE",FACE,{"disambiguationData":[OSD([subQ0])]})]});}
            var Q83;
            Q83=makeQuery(id+"F3.opExtrude","CAP_EDGE",EDGE,{"disambiguationData":[OSD([sQuery(id+"F0.wireOp",EDGE,"E0")])],"isStart":false});
            var Q84;
            {var subQ0=sQuery(id+"F2.wireOp",EDGE,"E30");Q84=makeQuery(id+"F3.opExtrude","CAP_EDGE",EDGE,{"disambiguationData":[OSD([subQ0]),TDD([makeQuery(id+"F2.imprint","IMPRINT",EDGE,{"disambiguationData":[TD([[makeQuery(id+"F2.imprint","INTERSECT",VERTEX,{"disambiguationData":[OD(0.0)],"derivedFrom":[makeQuery(id+"F1.opExtrude","CAP_EDGE",EDGE,{"disambiguationData":[OSD([sQuery(id+"F0.wireOp",EDGE,"E11.3.1")])],"isStart":false}),subQ0]}),-1.0]])],"derivedFrom":subQ0})])],"isStart":false});}
            var Q85;
            {var subQ0=sQuery(id+"F0.wireOp",EDGE,"E11.2.0");Q85=makeQuery(id+"F3.boolean.opBoolean","MERGE",FACE,{"derivedFrom":[makeQuery(id+"F1.opExtrude","SWEPT_FACE",FACE,{"disambiguationData":[OSD([subQ0])]}),makeQuery(id+"F3.opExtrude","SWEPT_FACE",FACE,{"disambiguationData":[OSD([subQ0])]})]});}
            var Q86;
            Q86=makeQuery(id+"F1.opExtrude","CAP_EDGE",EDGE,{"disambiguationData":[OSD([sQuery(id+"F0.wireOp",EDGE,"E7.3.1")])],"isStart":true});
            var Q87;
            {var subQ0=sQuery(id+"F2.wireOp",EDGE,"E30");var subQ1=sQuery(id+"F0.wireOp",EDGE,"E11.1.0");Q87=makeQuery(id+"F3.opExtrude","SWEPT_EDGE",EDGE,{"disambiguationData":[OSD([subQ1,subQ0]),TDD([makeQuery(id+"F2.imprint","INTERSECT",VERTEX,{"disambiguationData":[OD(1.0)],"derivedFrom":[makeQuery(id+"F1.opExtrude","CAP_EDGE",EDGE,{"disambiguationData":[OSD([subQ1])],"isStart":false}),subQ0]})])]});}
            var Q88;
            Q88=makeQuery(id+"F1.opExtrude","SWEPT_EDGE",EDGE,{"disambiguationData":[OSD([sQuery(id+"F0.wireOp",EDGE,"E7.2.1"),sQuery(id+"F0.wireOp",EDGE,"E11.2.0")])]});
            var Q89;
            {var subQ0=sQuery(id+"F2.wireOp",EDGE,"E30");var subQ1=sQuery(id+"F0.wireOp",EDGE,"E10.MirrorCS");Q89=makeQuery(id+"F3.opExtrude","SWEPT_EDGE",EDGE,{"disambiguationData":[OSD([subQ1,subQ0]),TDD([makeQuery(id+"F2.imprint","INTERSECT",VERTEX,{"disambiguationData":[OD(1.0)],"derivedFrom":[makeQuery(id+"F1.opExtrude","CAP_EDGE",EDGE,{"disambiguationData":[OSD([subQ1])],"isStart":false}),subQ0]})])]});}
            var Q90;
            Q90=makeQuery(id+"F1.opExtrude","CAP_EDGE",EDGE,{"disambiguationData":[OSD([sQuery(id+"F0.wireOp",EDGE,"E25.trimOffspring")])],"isStart":true});
            var Q91;
            Q91=makeQuery(id+"F1.opExtrude","SWEPT_EDGE",EDGE,{"disambiguationData":[OSD([sQuery(id+"F0.wireOp",EDGE,"E7.2.0"),sQuery(id+"F0.wireOp",EDGE,"E28.trimOffspring")])]});
            var Q92;
            Q92=makeQuery(id+"F1.opExtrude","SWEPT_EDGE",EDGE,{"disambiguationData":[OSD([sQuery(id+"F0.wireOp",EDGE,"E7.1.0"),sQuery(id+"F0.wireOp",EDGE,"E11.1.1")])]});
            var Q93;
            {var subQ0=sQuery(id+"F2.wireOp",EDGE,"E30");var subQ1=sQuery(id+"F0.wireOp",EDGE,"E11.4.0");Q93=makeQuery(id+"F3.opExtrude","SWEPT_EDGE",EDGE,{"disambiguationData":[OSD([subQ1,subQ0]),TDD([makeQuery(id+"F2.imprint","INTERSECT",VERTEX,{"disambiguationData":[OD(1.0)],"derivedFrom":[makeQuery(id+"F1.opExtrude","CAP_EDGE",EDGE,{"disambiguationData":[OSD([subQ1])],"isStart":false}),subQ0]})])]});}
            var Q94;
            {var subQ0=sQuery(id+"F2.wireOp",EDGE,"E30");var subQ1=sQuery(id+"F0.wireOp",EDGE,"E11.3.0");Q94=makeQuery(id+"F3.boolean.opBoolean","MERGE",EDGE,{"derivedFrom":[makeQuery(id+"F1.opExtrude","SWEPT_EDGE",EDGE,{"disambiguationData":[OSD([subQ1,sQuery(id+"F0.wireOp",EDGE,"E22.trimOffspring")])]}),makeQuery(id+"F3.opExtrude","SWEPT_EDGE",EDGE,{"disambiguationData":[OSD([subQ1,subQ0]),TDD([makeQuery(id+"F2.imprint","INTERSECT",VERTEX,{"disambiguationData":[OD(0.0)],"derivedFrom":[makeQuery(id+"F1.opExtrude","CAP_EDGE",EDGE,{"disambiguationData":[OSD([subQ1])],"isStart":false}),subQ0]})])]})]});}
            var Q95;
            Q95=makeQuery(id+"F3.opExtrude","CAP_EDGE",EDGE,{"disambiguationData":[OSD([sQuery(id+"F0.wireOp",EDGE,"E11.4.1")])],"isStart":false});
            var Q96;
            Q96=makeQuery(id+"F1.opExtrude","CAP_EDGE",EDGE,{"disambiguationData":[OSD([sQuery(id+"F0.wireOp",EDGE,"E11.4.0")])],"isStart":false});
            var Q97;
            {var subQ0=sQuery(id+"F2.wireOp",EDGE,"E30");Q97=makeQuery(id+"F3.opExtrude","CAP_EDGE",EDGE,{"disambiguationData":[OSD([subQ0]),TDD([makeQuery(id+"F2.imprint","IMPRINT",EDGE,{"disambiguationData":[TD([[makeQuery(id+"F2.imprint","INTERSECT",VERTEX,{"disambiguationData":[OD(1.0)],"derivedFrom":[makeQuery(id+"F1.opExtrude","CAP_EDGE",EDGE,{"disambiguationData":[OSD([sQuery(id+"F0.wireOp",EDGE,"E11.1.0")])],"isStart":false}),subQ0]}),-1.0]])],"derivedFrom":subQ0})])],"isStart":true});}
            var Q98;
            Q98=makeQuery(id+"F1.opExtrude","SWEPT_EDGE",EDGE,{"disambiguationData":[OSD([sQuery(id+"F0.wireOp",EDGE,"E3.left"),sQuery(id+"F0.wireOp",EDGE,"E10.MirrorCS")])]});
            var Q99;
            Q99=makeQuery(id+"F1.opExtrude","SWEPT_EDGE",EDGE,{"disambiguationData":[OSD([sQuery(id+"F0.wireOp",EDGE,"E7.3.1"),sQuery(id+"F0.wireOp",EDGE,"E28.trimOffspring")])]});
            var Q100;
            Q100=makeQuery(id+"F1.opExtrude","CAP_EDGE",EDGE,{"disambiguationData":[OSD([sQuery(id+"F0.wireOp",EDGE,"E11.3.1")])],"isStart":false});
            var Q101;
            {var subQ0=sQuery(id+"F2.wireOp",EDGE,"E30");var subQ1=sQuery(id+"F0.wireOp",EDGE,"E11.1.1");Q101=makeQuery(id+"F3.boolean.opBoolean","MERGE",EDGE,{"derivedFrom":[makeQuery(id+"F1.opExtrude","SWEPT_EDGE",EDGE,{"disambiguationData":[OSD([sQuery(id+"F0.wireOp",EDGE,"E8"),subQ1])]}),makeQuery(id+"F3.opExtrude","SWEPT_EDGE",EDGE,{"disambiguationData":[OSD([subQ1,subQ0]),TDD([makeQuery(id+"F2.imprint","INTERSECT",VERTEX,{"disambiguationData":[OD(0.0)],"derivedFrom":[makeQuery(id+"F1.opExtrude","CAP_EDGE",EDGE,{"disambiguationData":[OSD([subQ1])],"isStart":false}),subQ0]})])]})]});}
            var Q102;
            Q102=makeQuery(id+"F1.opExtrude","CAP_EDGE",EDGE,{"disambiguationData":[OSD([sQuery(id+"F0.wireOp",EDGE,"E11.1.1")])],"isStart":false});
            var Q103;
            {var subQ0=sQuery(id+"F2.wireOp",EDGE,"E30");var subQ1=sQuery(id+"F0.wireOp",EDGE,"E11.2.1");Q103=makeQuery(id+"F3.boolean.opBoolean","MERGE",EDGE,{"derivedFrom":[makeQuery(id+"F1.opExtrude","SWEPT_EDGE",EDGE,{"disambiguationData":[OSD([subQ1,sQuery(id+"F0.wireOp",EDGE,"E22.trimOffspring")])]}),makeQuery(id+"F3.opExtrude","SWEPT_EDGE",EDGE,{"disambiguationData":[OSD([subQ1,subQ0]),TDD([makeQuery(id+"F2.imprint","INTERSECT",VERTEX,{"disambiguationData":[OD(0.0)],"derivedFrom":[makeQuery(id+"F1.opExtrude","CAP_EDGE",EDGE,{"disambiguationData":[OSD([subQ1])],"isStart":false}),subQ0]})])]})]});}
            var Q104;
            Q104=makeQuery(id+"F1.opExtrude","SWEPT_EDGE",EDGE,{"disambiguationData":[OSD([sQuery(id+"F0.wireOp",EDGE,"E7.1.1"),sQuery(id+"F0.wireOp",EDGE,"E11.1.0")])]});
            var Q105;
            {var subQ0=sQuery(id+"F2.wireOp",EDGE,"E30");Q105=makeQuery(id+"F3.opExtrude","CAP_EDGE",EDGE,{"disambiguationData":[OSD([subQ0]),TDD([makeQuery(id+"F2.imprint","IMPRINT",EDGE,{"disambiguationData":[TD([[makeQuery(id+"F2.imprint","INTERSECT",VERTEX,{"disambiguationData":[OD(1.0)],"derivedFrom":[makeQuery(id+"F1.opExtrude","CAP_EDGE",EDGE,{"disambiguationData":[OSD([sQuery(id+"F0.wireOp",EDGE,"E11.4.0")])],"isStart":false}),subQ0]}),-1.0]])],"derivedFrom":subQ0})])],"isStart":false});}
            var Q106;
            {var subQ0=sQuery(id+"F2.wireOp",EDGE,"E30");var subQ1=sQuery(id+"F0.wireOp",EDGE,"E10.MirrorCS");Q106=makeQuery(id+"F3.boolean.opBoolean","MERGE",EDGE,{"derivedFrom":[makeQuery(id+"F1.opExtrude","SWEPT_EDGE",EDGE,{"disambiguationData":[OSD([subQ1,sQuery(id+"F0.wireOp",EDGE,"E16.trimOffspring")])]}),makeQuery(id+"F3.opExtrude","SWEPT_EDGE",EDGE,{"disambiguationData":[OSD([subQ1,subQ0]),TDD([makeQuery(id+"F2.imprint","INTERSECT",VERTEX,{"disambiguationData":[OD(0.0)],"derivedFrom":[makeQuery(id+"F1.opExtrude","CAP_EDGE",EDGE,{"disambiguationData":[OSD([subQ1])],"isStart":false}),subQ0]})])]})]});}
            var Q107;
            Q107=makeQuery(id+"F1.opExtrude","SWEPT_EDGE",EDGE,{"disambiguationData":[OSD([sQuery(id+"F0.wireOp",EDGE,"E7.3.0"),sQuery(id+"F0.wireOp",EDGE,"E27.trimOffspring")])]});
            var Q108;
            Q108=makeQuery(id+"F1.opExtrude","SWEPT_EDGE",EDGE,{"disambiguationData":[OSD([sQuery(id+"F0.wireOp",EDGE,"E7.3.1"),sQuery(id+"F0.wireOp",EDGE,"E11.3.0")])]});
            var Q109;
            Q109=makeQuery(id+"F1.opExtrude","CAP_EDGE",EDGE,{"disambiguationData":[OSD([sQuery(id+"F0.wireOp",EDGE,"E7.3.0")])],"isStart":true});
            var Q110;
            {var subQ0=sQuery(id+"F2.wireOp",EDGE,"E30");var subQ1=sQuery(id+"F0.wireOp",EDGE,"E11.1.1");Q110=makeQuery(id+"F3.opExtrude","SWEPT_EDGE",EDGE,{"disambiguationData":[OSD([subQ1,subQ0]),TDD([makeQuery(id+"F2.imprint","INTERSECT",VERTEX,{"disambiguationData":[OD(1.0)],"derivedFrom":[makeQuery(id+"F1.opExtrude","CAP_EDGE",EDGE,{"disambiguationData":[OSD([subQ1])],"isStart":false}),subQ0]})])]});}
            var Q111;
            Q111=makeQuery(id+"F1.opExtrude","SWEPT_EDGE",EDGE,{"disambiguationData":[OSD([sQuery(id+"F0.wireOp",EDGE,"E3.right"),sQuery(id+"F0.wireOp",EDGE,"E9")])]});
            var Q112;
            Q112=makeQuery(id+"F1.opExtrude","SWEPT_EDGE",EDGE,{"disambiguationData":[OSD([sQuery(id+"F0.wireOp",EDGE,"E7.4.0"),sQuery(id+"F0.wireOp",EDGE,"E11.4.1")])]});
            var Q113;
            {var subQ0=sQuery(id+"F2.wireOp",EDGE,"E30");var subQ1=sQuery(id+"F0.wireOp",EDGE,"E11.3.1");Q113=makeQuery(id+"F3.boolean.opBoolean","MERGE",EDGE,{"derivedFrom":[makeQuery(id+"F1.opExtrude","SWEPT_EDGE",EDGE,{"disambiguationData":[OSD([subQ1,sQuery(id+"F0.wireOp",EDGE,"E25.trimOffspring")])]}),makeQuery(id+"F3.opExtrude","SWEPT_EDGE",EDGE,{"disambiguationData":[OSD([subQ1,subQ0]),TDD([makeQuery(id+"F2.imprint","INTERSECT",VERTEX,{"disambiguationData":[OD(0.0)],"derivedFrom":[makeQuery(id+"F1.opExtrude","CAP_EDGE",EDGE,{"disambiguationData":[OSD([subQ1])],"isStart":false}),subQ0]})])]})]});}
            var Q114;
            Q114=makeQuery(id+"F1.opExtrude","CAP_EDGE",EDGE,{"disambiguationData":[OSD([sQuery(id+"F0.wireOp",EDGE,"E22.trimOffspring")])],"isStart":true});
            var Q115;
            Q115=makeQuery(id+"F3.opExtrude","CAP_EDGE",EDGE,{"disambiguationData":[OSD([sQuery(id+"F0.wireOp",EDGE,"E11.2.1")])],"isStart":false});
            var Q116;
            {var subQ0=sQuery(id+"F2.wireOp",EDGE,"E30");Q116=makeQuery(id+"F3.opExtrude","CAP_EDGE",EDGE,{"disambiguationData":[OSD([subQ0]),TDD([makeQuery(id+"F2.imprint","IMPRINT",EDGE,{"disambiguationData":[TD([[makeQuery(id+"F2.imprint","INTERSECT",VERTEX,{"disambiguationData":[OD(1.0)],"derivedFrom":[makeQuery(id+"F1.opExtrude","CAP_EDGE",EDGE,{"disambiguationData":[OSD([sQuery(id+"F0.wireOp",EDGE,"E11.3.0")])],"isStart":false}),subQ0]}),-1.0]])],"derivedFrom":subQ0})])],"isStart":true});}
            var Q117;
            {var subQ0=sQuery(id+"F2.wireOp",EDGE,"E30");Q117=makeQuery(id+"F3.opExtrude","SWEPT_FACE",FACE,{"disambiguationData":[OSD([subQ0]),TDD([makeQuery(id+"F2.imprint","IMPRINT",EDGE,{"disambiguationData":[TD([[makeQuery(id+"F2.imprint","INTERSECT",VERTEX,{"disambiguationData":[OD(1.0)],"derivedFrom":[makeQuery(id+"F1.opExtrude","CAP_EDGE",EDGE,{"disambiguationData":[OSD([sQuery(id+"F0.wireOp",EDGE,"E11.2.0")])],"isStart":false}),subQ0]}),-1.0]])],"derivedFrom":subQ0})])]});}
            var Q118;
            Q118=makeQuery(id+"F1.opExtrude","CAP_EDGE",EDGE,{"disambiguationData":[OSD([sQuery(id+"F0.wireOp",EDGE,"E16.trimOffspring")])],"isStart":true});
            var Q119;
            Q119=makeQuery(id+"F3.opExtrude","CAP_EDGE",EDGE,{"disambiguationData":[OSD([sQuery(id+"F0.wireOp",EDGE,"E9")])],"isStart":false});
            var Q120;
            {var subQ0=sQuery(id+"F2.wireOp",EDGE,"E30");var subQ1=sQuery(id+"F0.wireOp",EDGE,"E11.4.1");Q120=makeQuery(id+"F3.boolean.opBoolean","MERGE",EDGE,{"derivedFrom":[makeQuery(id+"F1.opExtrude","SWEPT_EDGE",EDGE,{"disambiguationData":[OSD([subQ1,sQuery(id+"F0.wireOp",EDGE,"E19.trimOffspring")])]}),makeQuery(id+"F3.opExtrude","SWEPT_EDGE",EDGE,{"disambiguationData":[OSD([subQ1,subQ0]),TDD([makeQuery(id+"F2.imprint","INTERSECT",VERTEX,{"disambiguationData":[OD(0.0)],"derivedFrom":[makeQuery(id+"F1.opExtrude","CAP_EDGE",EDGE,{"disambiguationData":[OSD([subQ1])],"isStart":false}),subQ0]})])]})]});}
            var Q121;
            {var subQ0=sQuery(id+"F2.wireOp",EDGE,"E30");var subQ1=sQuery(id+"F0.wireOp",EDGE,"E11.4.0");Q121=makeQuery(id+"F3.boolean.opBoolean","MERGE",EDGE,{"derivedFrom":[makeQuery(id+"F1.opExtrude","SWEPT_EDGE",EDGE,{"disambiguationData":[OSD([subQ1,sQuery(id+"F0.wireOp",EDGE,"E25.trimOffspring")])]}),makeQuery(id+"F3.opExtrude","SWEPT_EDGE",EDGE,{"disambiguationData":[OSD([subQ1,subQ0]),TDD([makeQuery(id+"F2.imprint","INTERSECT",VERTEX,{"disambiguationData":[OD(0.0)],"derivedFrom":[makeQuery(id+"F1.opExtrude","CAP_EDGE",EDGE,{"disambiguationData":[OSD([subQ1])],"isStart":false}),subQ0]})])]})]});}
            var Q122;
            {var subQ0=sQuery(id+"F2.wireOp",EDGE,"E30");Q122=makeQuery(id+"F3.opExtrude","CAP_EDGE",EDGE,{"disambiguationData":[OSD([subQ0]),TDD([makeQuery(id+"F2.imprint","IMPRINT",EDGE,{"disambiguationData":[TD([[makeQuery(id+"F2.imprint","INTERSECT",VERTEX,{"disambiguationData":[OD(1.0)],"derivedFrom":[makeQuery(id+"F1.opExtrude","CAP_EDGE",EDGE,{"disambiguationData":[OSD([sQuery(id+"F0.wireOp",EDGE,"E11.4.0")])],"isStart":false}),subQ0]}),-1.0]])],"derivedFrom":subQ0})])],"isStart":true});}
            var Q123;
            Q123=makeQuery(id+"F1.opExtrude","CAP_EDGE",EDGE,{"disambiguationData":[OSD([sQuery(id+"F0.wireOp",EDGE,"E11.4.1")])],"isStart":false});
            var Q124;
            Q124=makeQuery(id+"F3.opExtrude","CAP_EDGE",EDGE,{"disambiguationData":[OSD([sQuery(id+"F0.wireOp",EDGE,"E11.1.1")])],"isStart":false});
            var Q125;
            Q125=makeQuery(id+"F1.opExtrude","CAP_EDGE",EDGE,{"disambiguationData":[OSD([sQuery(id+"F0.wireOp",EDGE,"E11.1.0")])],"isStart":false});
            var Q126;
            {var subQ0=sQuery(id+"F2.wireOp",EDGE,"E30");var subQ1=sQuery(id+"F0.wireOp",EDGE,"E11.3.0");Q126=makeQuery(id+"F3.opExtrude","SWEPT_EDGE",EDGE,{"disambiguationData":[OSD([subQ1,subQ0]),TDD([makeQuery(id+"F2.imprint","INTERSECT",VERTEX,{"disambiguationData":[OD(1.0)],"derivedFrom":[makeQuery(id+"F1.opExtrude","CAP_EDGE",EDGE,{"disambiguationData":[OSD([subQ1])],"isStart":false}),subQ0]})])]});}
            var Q127;
            {var subQ0=sQuery(id+"F2.wireOp",EDGE,"E30");Q127=makeQuery(id+"F3.opExtrude","CAP_EDGE",EDGE,{"disambiguationData":[OSD([subQ0]),TDD([makeQuery(id+"F2.imprint","IMPRINT",EDGE,{"disambiguationData":[TD([[makeQuery(id+"F2.imprint","INTERSECT",VERTEX,{"disambiguationData":[OD(1.0)],"derivedFrom":[makeQuery(id+"F1.opExtrude","CAP_EDGE",EDGE,{"disambiguationData":[OSD([sQuery(id+"F0.wireOp",EDGE,"E9")])],"isStart":false}),subQ0]}),-1.0]])],"derivedFrom":subQ0})])],"isStart":true});}
            var Q128;
            Q128=makeQuery(id+"F1.opExtrude","CAP_EDGE",EDGE,{"disambiguationData":[OSD([sQuery(id+"F0.wireOp",EDGE,"E10.MirrorCS")])],"isStart":false});
            var Q129;
            Q129=makeQuery(id+"F1.opExtrude","CAP_EDGE",EDGE,{"disambiguationData":[OSD([sQuery(id+"F0.wireOp",EDGE,"E9")])],"isStart":false});
            var Q130;
            {var subQ0=sQuery(id+"F2.wireOp",EDGE,"E30");Q130=makeQuery(id+"F3.opExtrude","CAP_EDGE",EDGE,{"disambiguationData":[OSD([subQ0]),TDD([makeQuery(id+"F2.imprint","IMPRINT",EDGE,{"disambiguationData":[TD([[makeQuery(id+"F2.imprint","INTERSECT",VERTEX,{"disambiguationData":[OD(1.0)],"derivedFrom":[makeQuery(id+"F1.opExtrude","CAP_EDGE",EDGE,{"disambiguationData":[OSD([sQuery(id+"F0.wireOp",EDGE,"E11.3.0")])],"isStart":false}),subQ0]}),-1.0]])],"derivedFrom":subQ0})])],"isStart":false});}
            var Q131;
            Q131=makeQuery(id+"F3.opExtrude","CAP_EDGE",EDGE,{"disambiguationData":[OSD([sQuery(id+"F0.wireOp",EDGE,"E11.3.0")])],"isStart":false});
            var Q132;
            {var subQ0=sQuery(id+"F2.wireOp",EDGE,"E30");var subQ1=sQuery(id+"F0.wireOp",EDGE,"E11.1.0");Q132=makeQuery(id+"F3.boolean.opBoolean","MERGE",EDGE,{"derivedFrom":[makeQuery(id+"F1.opExtrude","SWEPT_EDGE",EDGE,{"disambiguationData":[OSD([subQ1,sQuery(id+"F0.wireOp",EDGE,"E16.trimOffspring")])]}),makeQuery(id+"F3.opExtrude","SWEPT_EDGE",EDGE,{"disambiguationData":[OSD([subQ1,subQ0]),TDD([makeQuery(id+"F2.imprint","INTERSECT",VERTEX,{"disambiguationData":[OD(0.0)],"derivedFrom":[makeQuery(id+"F1.opExtrude","CAP_EDGE",EDGE,{"disambiguationData":[OSD([subQ1])],"isStart":false}),subQ0]})])]})]});}
            var Q133;
            Q133=makeQuery(id+"F3.opExtrude","CAP_EDGE",EDGE,{"disambiguationData":[OSD([sQuery(id+"F0.wireOp",EDGE,"E11.3.1")])],"isStart":false});
            var Q134;
            Q134=makeQuery(id+"F3.opExtrude","CAP_EDGE",EDGE,{"disambiguationData":[OSD([sQuery(id+"F0.wireOp",EDGE,"E11.2.0")])],"isStart":false});
            var Q135;
            {var subQ0=sQuery(id+"F2.wireOp",EDGE,"E30");var subQ1=sQuery(id+"F0.wireOp",EDGE,"E11.3.1");Q135=makeQuery(id+"F3.opExtrude","SWEPT_EDGE",EDGE,{"disambiguationData":[OSD([subQ1,subQ0]),TDD([makeQuery(id+"F2.imprint","INTERSECT",VERTEX,{"disambiguationData":[OD(1.0)],"derivedFrom":[makeQuery(id+"F1.opExtrude","CAP_EDGE",EDGE,{"disambiguationData":[OSD([subQ1])],"isStart":false}),subQ0]})])]});}
            var Q136;
            {var subQ0=sQuery(id+"F2.wireOp",EDGE,"E30");var subQ1=sQuery(id+"F0.wireOp",EDGE,"E9");Q136=makeQuery(id+"F3.opExtrude","SWEPT_EDGE",EDGE,{"disambiguationData":[OSD([subQ1,subQ0]),TDD([makeQuery(id+"F2.imprint","INTERSECT",VERTEX,{"disambiguationData":[OD(1.0)],"derivedFrom":[makeQuery(id+"F1.opExtrude","CAP_EDGE",EDGE,{"disambiguationData":[OSD([subQ1])],"isStart":false}),subQ0]})])]});}
            var Q137;
            {var subQ0=sQuery(id+"F2.wireOp",EDGE,"E30");var subQ1=sQuery(id+"F0.wireOp",EDGE,"E9");Q137=makeQuery(id+"F3.boolean.opBoolean","MERGE",EDGE,{"derivedFrom":[makeQuery(id+"F1.opExtrude","SWEPT_EDGE",EDGE,{"disambiguationData":[OSD([subQ1,sQuery(id+"F0.wireOp",EDGE,"E19.trimOffspring")])]}),makeQuery(id+"F3.opExtrude","SWEPT_EDGE",EDGE,{"disambiguationData":[OSD([subQ1,subQ0]),TDD([makeQuery(id+"F2.imprint","INTERSECT",VERTEX,{"disambiguationData":[OD(0.0)],"derivedFrom":[makeQuery(id+"F1.opExtrude","CAP_EDGE",EDGE,{"disambiguationData":[OSD([subQ1])],"isStart":false}),subQ0]})])]})]});}
            var Q138;
            Q138=makeQuery(id+"F1.opExtrude","SWEPT_EDGE",EDGE,{"disambiguationData":[OSD([sQuery(id+"F0.wireOp",EDGE,"E7.3.0"),sQuery(id+"F0.wireOp",EDGE,"E11.3.1")])]});
            var Q139;
            Q139=makeQuery(id+"F1.opExtrude","CAP_EDGE",EDGE,{"disambiguationData":[OSD([sQuery(id+"F0.wireOp",EDGE,"E11.3.0")])],"isStart":false});
            var Q140;
            Q140=makeQuery(id+"F1.opExtrude","SWEPT_EDGE",EDGE,{"disambiguationData":[OSD([sQuery(id+"F0.wireOp",EDGE,"E7.2.0"),sQuery(id+"F0.wireOp",EDGE,"E11.2.1")])]});
            var Q141;
            Q141=makeQuery(id+"F1.opExtrude","CAP_EDGE",EDGE,{"disambiguationData":[OSD([sQuery(id+"F0.wireOp",EDGE,"E8")])],"isStart":true});
            var Q142;
            {var subQ0=sQuery(id+"F2.wireOp",EDGE,"E30");var subQ1=sQuery(id+"F0.wireOp",EDGE,"E11.2.1");Q142=makeQuery(id+"F3.opExtrude","SWEPT_EDGE",EDGE,{"disambiguationData":[OSD([subQ1,subQ0]),TDD([makeQuery(id+"F2.imprint","INTERSECT",VERTEX,{"disambiguationData":[OD(1.0)],"derivedFrom":[makeQuery(id+"F1.opExtrude","CAP_EDGE",EDGE,{"disambiguationData":[OSD([subQ1])],"isStart":false}),subQ0]})])]});}
            var Q143;
            Q143=makeQuery(id+"F1.opExtrude","CAP_EDGE",EDGE,{"disambiguationData":[OSD([sQuery(id+"F0.wireOp",EDGE,"E11.2.1")])],"isStart":false});
            var Q144;
            Q144=makeQuery(id+"F1.opExtrude","CAP_EDGE",EDGE,{"disambiguationData":[OSD([sQuery(id+"F0.wireOp",EDGE,"E0")])],"isStart":true});
            var Q145;
            Q145=makeQuery(id+"F3.opExtrude","CAP_EDGE",EDGE,{"disambiguationData":[OSD([sQuery(id+"F0.wireOp",EDGE,"E11.1.0")])],"isStart":false});
            var Q146;
            {var subQ0=sQuery(id+"F2.wireOp",EDGE,"E30");Q146=makeQuery(id+"F3.opExtrude","CAP_EDGE",EDGE,{"disambiguationData":[OSD([subQ0]),TDD([makeQuery(id+"F2.imprint","IMPRINT",EDGE,{"disambiguationData":[TD([[makeQuery(id+"F2.imprint","INTERSECT",VERTEX,{"disambiguationData":[OD(0.0)],"derivedFrom":[makeQuery(id+"F1.opExtrude","CAP_EDGE",EDGE,{"disambiguationData":[OSD([sQuery(id+"F0.wireOp",EDGE,"E10.MirrorCS")])],"isStart":false}),subQ0]}),-1.0]])],"derivedFrom":subQ0})])],"isStart":false});}
            var Q147;
            {var subQ0=sQuery(id+"F2.wireOp",EDGE,"E30");var subQ1=sQuery(id+"F0.wireOp",EDGE,"E11.4.1");Q147=makeQuery(id+"F3.opExtrude","SWEPT_EDGE",EDGE,{"disambiguationData":[OSD([subQ1,subQ0]),TDD([makeQuery(id+"F2.imprint","INTERSECT",VERTEX,{"disambiguationData":[OD(1.0)],"derivedFrom":[makeQuery(id+"F1.opExtrude","CAP_EDGE",EDGE,{"disambiguationData":[OSD([subQ1])],"isStart":false}),subQ0]})])]});}
            var Q148;
            {var subQ0=sQuery(id+"F2.wireOp",EDGE,"E30");Q148=makeQuery(id+"F3.opExtrude","CAP_EDGE",EDGE,{"disambiguationData":[OSD([subQ0]),TDD([makeQuery(id+"F2.imprint","IMPRINT",EDGE,{"disambiguationData":[TD([[makeQuery(id+"F2.imprint","INTERSECT",VERTEX,{"disambiguationData":[OD(1.0)],"derivedFrom":[makeQuery(id+"F1.opExtrude","CAP_EDGE",EDGE,{"disambiguationData":[OSD([sQuery(id+"F0.wireOp",EDGE,"E11.2.0")])],"isStart":false}),subQ0]}),-1.0]])],"derivedFrom":subQ0})])],"isStart":true});}
            var Q149;
            {var subQ0=sQuery(id+"F2.wireOp",EDGE,"E30");Q149=makeQuery(id+"F3.opExtrude","CAP_EDGE",EDGE,{"disambiguationData":[OSD([subQ0]),TDD([makeQuery(id+"F2.imprint","IMPRINT",EDGE,{"disambiguationData":[TD([[makeQuery(id+"F2.imprint","INTERSECT",VERTEX,{"disambiguationData":[OD(1.0)],"derivedFrom":[makeQuery(id+"F1.opExtrude","CAP_EDGE",EDGE,{"disambiguationData":[OSD([sQuery(id+"F0.wireOp",EDGE,"E11.2.0")])],"isStart":false}),subQ0]}),-1.0]])],"derivedFrom":subQ0})])],"isStart":false});}
            var Q150;
            {var subQ0=sQuery(id+"F2.wireOp",EDGE,"E30");var subQ1=sQuery(id+"F0.wireOp",EDGE,"E11.2.0");Q150=makeQuery(id+"F3.opExtrude","SWEPT_EDGE",EDGE,{"disambiguationData":[OSD([subQ1,subQ0]),TDD([makeQuery(id+"F2.imprint","INTERSECT",VERTEX,{"disambiguationData":[OD(1.0)],"derivedFrom":[makeQuery(id+"F1.opExtrude","CAP_EDGE",EDGE,{"disambiguationData":[OSD([subQ1])],"isStart":false}),subQ0]})])]});}
            var Q151;
            Q151=makeQuery(id+"F3.opExtrude","CAP_EDGE",EDGE,{"disambiguationData":[OSD([sQuery(id+"F0.wireOp",EDGE,"E10.MirrorCS")])],"isStart":false});
            var Q152;
            Q152=makeQuery(id+"F1.opExtrude","CAP_EDGE",EDGE,{"disambiguationData":[OSD([sQuery(id+"F0.wireOp",EDGE,"E19.trimOffspring")])],"isStart":true});
            var Q153;
            Q153=makeQuery(id+"F1.opExtrude","CAP_EDGE",EDGE,{"disambiguationData":[OSD([sQuery(id+"F0.wireOp",EDGE,"E11.4.1")])],"isStart":true});
            var Q154;
            Q154=makeQuery(id+"F1.opExtrude","CAP_EDGE",EDGE,{"disambiguationData":[OSD([sQuery(id+"F0.wireOp",EDGE,"E11.1.0")])],"isStart":true});
            var Q155;
            Q155=makeQuery(id+"F1.opExtrude","CAP_EDGE",EDGE,{"disambiguationData":[OSD([sQuery(id+"F0.wireOp",EDGE,"E11.2.1")])],"isStart":true});
            var Q156;
            Q156=makeQuery(id+"F1.opExtrude","CAP_EDGE",EDGE,{"disambiguationData":[OSD([sQuery(id+"F0.wireOp",EDGE,"E11.4.0")])],"isStart":true});
            var Q157;
            Q157=makeQuery(id+"F1.opExtrude","CAP_EDGE",EDGE,{"disambiguationData":[OSD([sQuery(id+"F0.wireOp",EDGE,"E11.1.1")])],"isStart":true});
            var Q158;
            Q158=makeQuery(id+"F1.opExtrude","CAP_EDGE",EDGE,{"disambiguationData":[OSD([sQuery(id+"F0.wireOp",EDGE,"E11.3.1")])],"isStart":true});
            var Q159;
            Q159=makeQuery(id+"F1.opExtrude","CAP_EDGE",EDGE,{"disambiguationData":[OSD([sQuery(id+"F0.wireOp",EDGE,"E11.2.0")])],"isStart":false});
            var Q160;
            Q160=makeQuery(id+"F1.opExtrude","CAP_EDGE",EDGE,{"disambiguationData":[OSD([sQuery(id+"F0.wireOp",EDGE,"E10.MirrorCS")])],"isStart":true});
            var Q161;
            Q161=makeQuery(id+"F1.opExtrude","CAP_EDGE",EDGE,{"disambiguationData":[OSD([sQuery(id+"F0.wireOp",EDGE,"E11.3.0")])],"isStart":true});
            var Q162;
            Q162=makeQuery(id+"F1.opExtrude","CAP_EDGE",EDGE,{"disambiguationData":[OSD([sQuery(id+"F0.wireOp",EDGE,"E11.2.0")])],"isStart":true});
            var Q163;
            Q163=makeQuery(id+"F1.opExtrude","CAP_EDGE",EDGE,{"disambiguationData":[OSD([sQuery(id+"F0.wireOp",EDGE,"E9")])],"isStart":true});
            fillet(context, id + "F4", {"entities" : qUnion([Q0, Q1, Q2, Q3, Q4, Q5, Q6, Q7, Q8, Q9, Q10, Q11, Q12, Q13, Q14, Q15, Q16, Q17, Q18, Q19, Q20, Q21, Q22, Q23, Q24, Q25, Q26, Q27, Q28, Q29, Q30, Q31, Q32, Q33, Q34, Q35, Q36, Q37, Q38, Q39, Q40, Q41, Q42, Q43, Q44, Q45, Q46, Q47, Q48, Q49, Q50, Q51, Q52, Q53, Q54, Q55, Q56, Q57, Q58, Q59, Q60, Q61, Q62, Q63, Q64, Q65, Q66, Q67, Q68, Q69, Q70, Q71, Q72, Q73, Q74, Q75, Q76, Q77, Q78, Q79, Q80, Q81, Q82, Q83, Q84, Q85, Q86, Q87, Q88, Q89, Q90, Q91, Q92, Q93, Q94, Q95, Q96, Q97, Q98, Q99, Q100, Q101, Q102, Q103, Q104, Q105, Q106, Q107, Q108, Q109, Q110, Q111, Q112, Q113, Q114, Q115, Q116, Q117, Q118, Q119, Q120, Q121, Q122, Q123, Q124, Q125, Q126, Q127, Q128, Q129, Q130, Q131, Q132, Q133, Q134, Q135, Q136, Q137, Q138, Q139, Q140, Q141, Q142, Q143, Q144, Q145, Q146, Q147, Q148, Q149, Q150, Q151, Q152, Q153, Q154, Q155, Q156, Q157, Q158, Q159, Q160, Q161, Q162, Q163]), "radius" : 1 * mm, "tangentPropagation" : true, "allowEdgeOverflow" : false});
        }
    });
